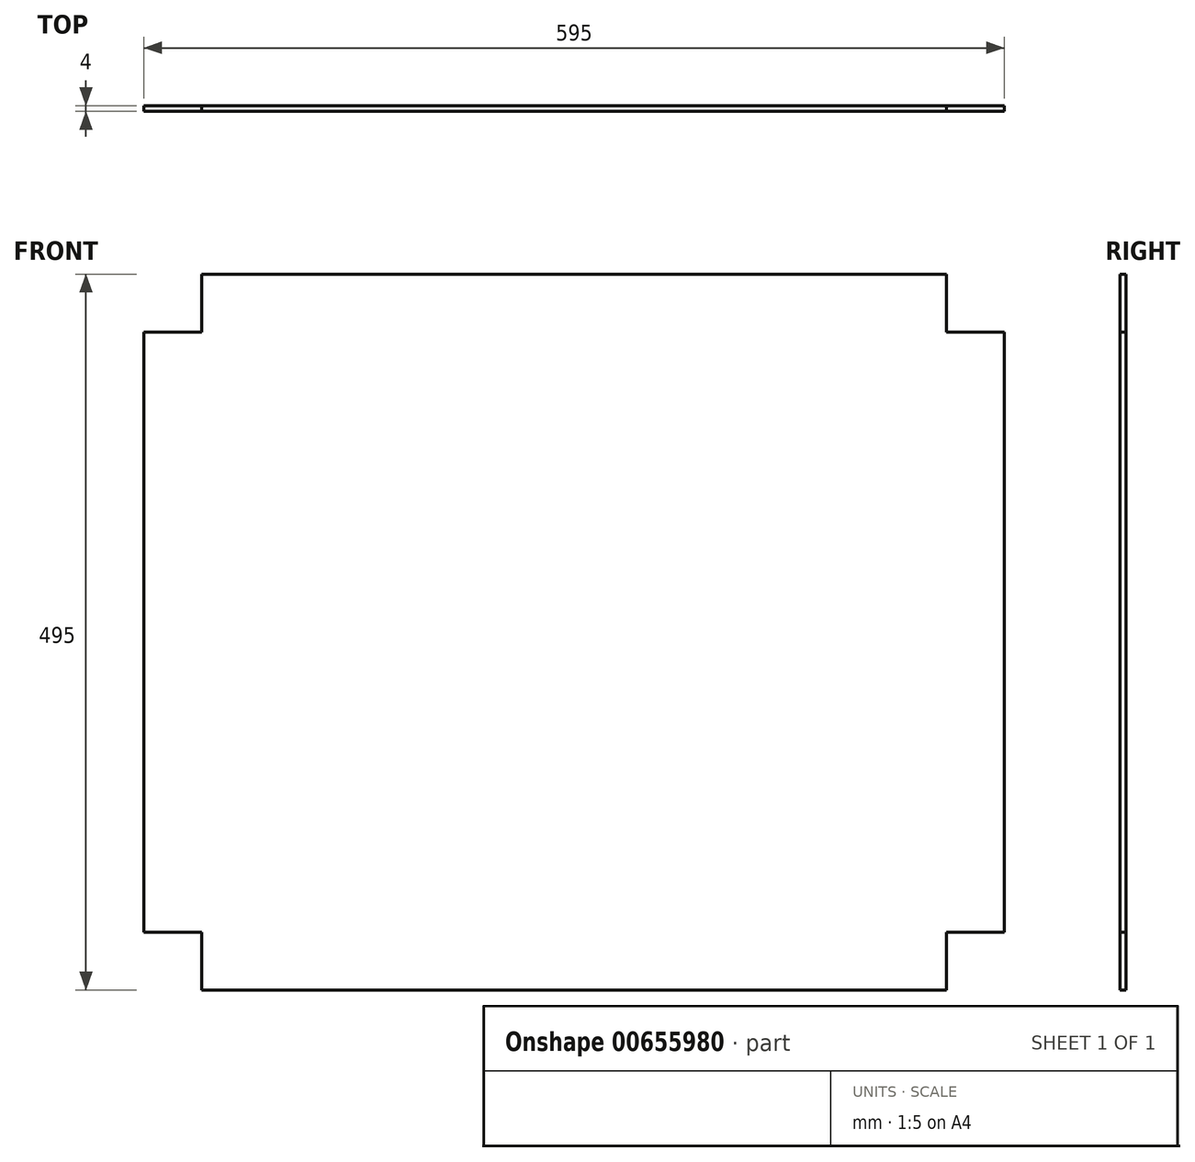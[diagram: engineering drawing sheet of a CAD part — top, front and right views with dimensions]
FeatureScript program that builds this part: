
annotation { "Feature Type Name" : "Feature", "Feature Type Description" : "" }
export const myFeature = defineFeature(function(context is Context, id is Id, definition is map)
    precondition{}
    {
        {
            var Q0;
            Q0=qCreatedBy(makeId("Front.planeOp"),FACE);
            var sketch = newSketch(context, id + "F0", { "sketchPlane" : qUnion([Q0])});
            skLineSegment(sketch, "E0", {"start": v(0, 247.5) * mm, "end": v(-257.5, 247.5) * mm});
            skLineSegment(sketch, "E1", {"start": v(-257.5, 247.5) * mm, "end": v(-257.5, 207.5) * mm});
            skLineSegment(sketch, "E2", {"start": v(-257.5, 207.5) * mm, "end": v(-297.5, 207.5) * mm});
            skLineSegment(sketch, "E3", {"start": v(-297.5, 207.5) * mm, "end": v(-297.5, 0) * mm});
            skLineSegment(sketch, "E4.MirrorCS", {"start": v(0, 247.5) * mm, "end": v(257.5, 247.5) * mm});
            skLineSegment(sketch, "E5.MirrorCS", {"start": v(257.5, 247.5) * mm, "end": v(257.5, 207.5) * mm});
            skLineSegment(sketch, "E6.MirrorCS", {"start": v(257.5, 207.5) * mm, "end": v(297.5, 207.5) * mm});
            skLineSegment(sketch, "E7.MirrorCS", {"start": v(297.5, 207.5) * mm, "end": v(297.5, 0) * mm});
            skLineSegment(sketch, "E8.MirrorCS", {"start": v(-297.5, -207.5) * mm, "end": v(-297.5, 0) * mm});
            skLineSegment(sketch, "E9.MirrorCS", {"start": v(-257.5, -207.5) * mm, "end": v(-297.5, -207.5) * mm});
            skLineSegment(sketch, "E10.MirrorCS", {"start": v(-257.5, -247.5) * mm, "end": v(-257.5, -207.5) * mm});
            skLineSegment(sketch, "E11.MirrorCS", {"start": v(0, -247.5) * mm, "end": v(-257.5, -247.5) * mm});
            skLineSegment(sketch, "E12.MirrorCS", {"start": v(0, -247.5) * mm, "end": v(257.5, -247.5) * mm});
            skLineSegment(sketch, "E13.MirrorCS", {"start": v(257.5, -247.5) * mm, "end": v(257.5, -207.5) * mm});
            skLineSegment(sketch, "E14.MirrorCS", {"start": v(257.5, -207.5) * mm, "end": v(297.5, -207.5) * mm});
            skLineSegment(sketch, "E15.MirrorCS", {"start": v(297.5, -207.5) * mm, "end": v(297.5, 0) * mm});
            skSolve(sketch);
        }
        {
            var Q0;
            Q0=makeQuery(id+"F0.imprint","IMPRINT",FACE,{"disambiguationData":[TD([[makeQuery(id+"F0.imprint","IMPRINT",EDGE,{"derivedFrom":sQuery(id+"F0.wireOp",EDGE,"E0")}),1.0]])]});
            extrude(context, id + "F1", {"entities" : qUnion([Q0]), "depth" : 4 * mm, "offsetDistance" : 25.4 * mm});
        }
    });
